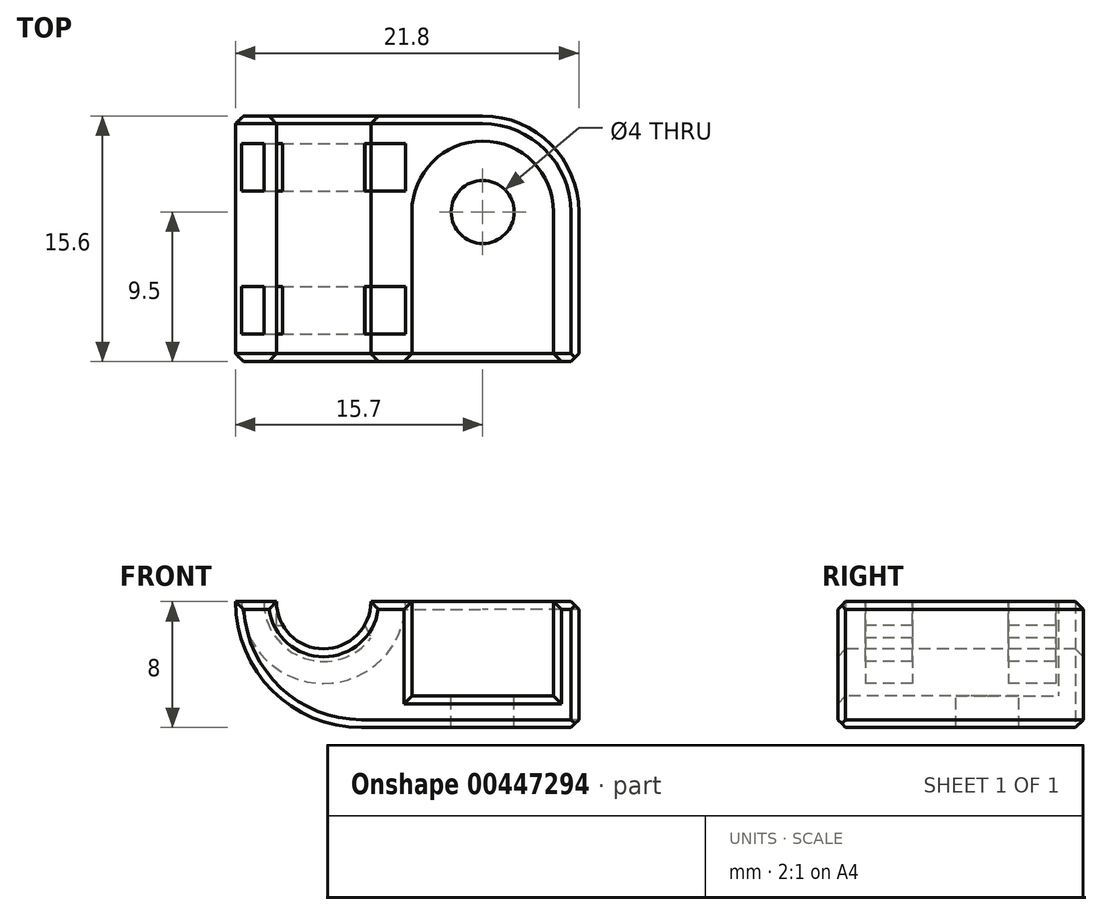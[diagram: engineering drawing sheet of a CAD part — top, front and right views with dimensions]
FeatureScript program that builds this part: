
annotation { "Feature Type Name" : "Feature", "Feature Type Description" : "" }
export const myFeature = defineFeature(function(context is Context, id is Id, definition is map)
    precondition{}
    {
        {
            var Q0;
            Q0=qCreatedBy(makeId("Top.planeOp"),FACE);
            var sketch = newSketch(context, id + "F0", { "sketchPlane" : qUnion([Q0])});
            skCircle(sketch, "E0", {"center": v(0, 0) * mm, "radius": 4.5 * mm});
            skLineSegment(sketch, "E1", {"start": v(-4.5, 0) * mm, "end": v(-4.5, -9.5) * mm});
            skLineSegment(sketch, "E2", {"start": v(-4.5, -9.5) * mm, "end": v(4.5, -9.5) * mm});
            skLineSegment(sketch, "E3", {"start": v(4.5, -9.5) * mm, "end": v(4.5, 0) * mm});
            skCircle(sketch, "E4", {"center": v(0, 0) * mm, "radius": 2 * mm});
            skSolve(sketch);
        }
        {
            var Q0;
            Q0=makeQuery(id+"F0.imprint","IMPRINT",FACE,{"disambiguationData":[TD([[makeQuery(id+"F0.imprint","IMPRINT",EDGE,{"derivedFrom":sQuery(id+"F0.wireOp",EDGE,"E4")}),-1.0]])]});
            var Q1;
            {var subQ0=sQuery(id+"F0.wireOp",EDGE,"E1");Q1=makeQuery(id+"F0.imprint","IMPRINT",FACE,{"disambiguationData":[TD([[makeQuery(id+"F0.imprint","IMPRINT",EDGE,{"derivedFrom":subQ0}),1.0]])]});}
            extrude(context, id + "F1", {"entities" : qUnion([Q0, Q1]), "depth" : 6 * mm});
        }
        {
            var Q0;
            Q0=qCreatedBy(makeId("Top.planeOp"),FACE);
            var sketch = newSketch(context, id + "F2", { "sketchPlane" : qUnion([Q0])});
            skLineSegment(sketch, "E5.bottom", {"start": v(6.1, -9.5) * mm, "end": v(-15.7, -9.5) * mm});
            skLineSegment(sketch, "E5.top", {"start": v(0, 6.1) * mm, "end": v(-15.7, 6.1) * mm});
            skLineSegment(sketch, "E5.left", {"start": v(6.1, -9.5) * mm, "end": v(6.1, 0) * mm});
            skLineSegment(sketch, "E5.right", {"start": v(-15.7, -9.5) * mm, "end": v(-15.7, 6.1) * mm});
            skPoint(sketch, "E6.visualSharp", {"position": v(6.1, 6.1) * mm});
            skArc(sketch, "E6.filletArc", {"start": v(6.1, 0) * mm, "mid": v(4.31, 4.31) * mm, "end": v(0, 6.1) * mm});
            skSolve(sketch);
        }
        {
            var Q0;
            Q0=makeQuery(id+"F2.imprint","IMPRINT",FACE,{"disambiguationData":[TD([[makeQuery(id+"F2.imprint","IMPRINT",EDGE,{"derivedFrom":sQuery(id+"F2.wireOp",EDGE,"E5.bottom")}),-1.0]])]});
            extrude(context, id + "F3", {"entities" : qUnion([Q0]), "depth" : 6 * mm, "hasSecondDirection" : true, "secondDirectionOppositeDirection" : true, "secondDirectionDepth" : 2 * mm});
        }
        {
            var Q0;
            Q0=makeQuery(id+"F3.opExtrude","SWEPT_FACE",FACE,{"disambiguationData":[OSD([sQuery(id+"F2.wireOp",EDGE,"E5.bottom")])]});
            var sketch = newSketch(context, id + "F4", { "sketchPlane" : qUnion([Q0])});
            skCircle(sketch, "E7", {"center": v(-10.1, 6) * mm, "radius": 3 * mm});
            skSolve(sketch);
        }
        {
            var Q0;
            {var subQ0=sQuery(id+"F4.wireOp",EDGE,"E7");var subQ1=makeQuery(id+"F3.opExtrude","CAP_EDGE",EDGE,{"disambiguationData":[OSD([sQuery(id+"F2.wireOp",EDGE,"E5.bottom")])],"isStart":false});var subQ2=makeQuery(id+"F4.imprint","INTERSECT",VERTEX,{"disambiguationData":[OD(0.0)],"derivedFrom":[subQ1,subQ0]});Q0=makeQuery(id+"F4.imprint","IMPRINT",FACE,{"disambiguationData":[TD([[makeQuery(id+"F4.imprint","IMPRINT",EDGE,{"disambiguationData":[TD([[subQ2,1.0]])],"derivedFrom":subQ0}),1.0]])]});}
            extrude(context, id + "F5", {"entities" : qUnion([Q0]), "operationType" : NewBodyOperationType.REMOVE, "oppositeDirection" : true, "depth" : 25 * mm});
        }
        {
            var Q0;
            {var subQ0=sQuery(id+"F2.wireOp",EDGE,"E5.bottom");var subQ1=sQuery(id+"F2.wireOp",EDGE,"E5.right");var subQ2=sQuery(id+"F2.wireOp",EDGE,"E5.top");Q0=makeQuery(id+"F5.boolean.opBoolean","SPLIT",FACE,{"disambiguationData":[TD([makeQuery(id+"F3.opExtrude","SWEPT_FACE",FACE,{"disambiguationData":[OSD([subQ1])]})])],"derivedFrom":makeQuery(id+"F3.opExtrude","CAP_FACE",FACE,{"disambiguationData":[OSD([subQ0,subQ2,sQuery(id+"F2.wireOp",EDGE,"E5.left"),subQ1,sQuery(id+"F2.wireOp",EDGE,"E6.filletArc")])],"isStart":false})});}
            var sketch = newSketch(context, id + "F6", { "sketchPlane" : qUnion([Q0])});
            skLineSegment(sketch, "E8", {"start": v(-10.1, 8.12) * mm, "end": v(-10.1, -13.09) * mm, "construction": true});
            skLineSegment(sketch, "E9.bottom", {"start": v(-15.3, -4.74) * mm, "end": v(-13.9, -4.74) * mm});
            skLineSegment(sketch, "E9.top", {"start": v(-15.3, -7.74) * mm, "end": v(-13.9, -7.74) * mm});
            skLineSegment(sketch, "E9.left", {"start": v(-15.3, -4.74) * mm, "end": v(-15.3, -7.74) * mm});
            skLineSegment(sketch, "E9.right", {"start": v(-13.9, -4.74) * mm, "end": v(-13.9, -7.74) * mm});
            skLineSegment(sketch, "E10.bottom", {"start": v(-15.3, 4.34) * mm, "end": v(-13.9, 4.34) * mm});
            skLineSegment(sketch, "E10.top", {"start": v(-15.3, 1.34) * mm, "end": v(-13.9, 1.34) * mm});
            skLineSegment(sketch, "E10.left", {"start": v(-15.3, 4.34) * mm, "end": v(-15.3, 1.34) * mm});
            skLineSegment(sketch, "E10.right", {"start": v(-13.9, 4.34) * mm, "end": v(-13.9, 1.34) * mm});
            skLineSegment(sketch, "E11", {"start": v(-15.7, -1.7) * mm, "end": v(-11.9, -1.7) * mm, "construction": true});
            skSolve(sketch);
        }
        {
            var Q0;
            Q0=makeQuery(id+"F6.imprint","IMPRINT",FACE,{"disambiguationData":[TD([[makeQuery(id+"F6.imprint","IMPRINT",EDGE,{"derivedFrom":sQuery(id+"F6.wireOp",EDGE,"E10.bottom")}),-1.0]])]});
            var Q1;
            Q1=makeQuery(id+"F6.imprint","IMPRINT",FACE,{"disambiguationData":[TD([[makeQuery(id+"F6.imprint","IMPRINT",EDGE,{"derivedFrom":sQuery(id+"F6.wireOp",EDGE,"E9.bottom")}),-1.0]])]});
            var Q2;
            Q2=sQuery(id+"F6.wireOp",EDGE,"E8");
            revolve(context, id + "F7", {"operationType" : NewBodyOperationType.REMOVE, "entities" : qUnion([Q0, Q1]), "axis" : qUnion([Q2]), "revolveType" : RevolveType.FULL, "oppositeDirection" : true});
        }
        {
            var Q0;
            Q0=makeQuery(id+"F1.opExtrude","SWEPT_BODY",BODY,{"disambiguationData":[OSD([sQuery(id+"F0.wireOp",EDGE,"E0"),sQuery(id+"F0.wireOp",EDGE,"E1"),sQuery(id+"F0.wireOp",EDGE,"E2"),sQuery(id+"F0.wireOp",EDGE,"E3"),sQuery(id+"F0.wireOp",EDGE,"E4")])]});
            var Q1;
            Q1=makeQuery(id+"F3.opExtrude","SWEPT_BODY",BODY,{"disambiguationData":[OSD([sQuery(id+"F2.wireOp",EDGE,"E5.bottom"),sQuery(id+"F2.wireOp",EDGE,"E5.top"),sQuery(id+"F2.wireOp",EDGE,"E5.left"),sQuery(id+"F2.wireOp",EDGE,"E5.right"),sQuery(id+"F2.wireOp",EDGE,"E6.filletArc")])]});
            booleanBodies(context, id + "F8", {"operationType" : BooleanOperationType.SUBTRACTION, "tools" : qUnion([Q0]), "targets" : qUnion([Q1])});
        }
        {
            var Q0;
            {var subQ0=sQuery(id+"F2.wireOp",EDGE,"E6.filletArc");var subQ1=sQuery(id+"F2.wireOp",EDGE,"E5.left");var subQ2=sQuery(id+"F2.wireOp",EDGE,"E5.top");var subQ3=sQuery(id+"F2.wireOp",EDGE,"E5.bottom");Q0=makeQuery(id+"F8.opBoolean","SPLIT",FACE,{"disambiguationData":[TD([makeQuery(id+"F1.opExtrude","SWEPT_FACE",FACE,{"disambiguationData":[OSD([sQuery(id+"F0.wireOp",EDGE,"E4")])]})])],"derivedFrom":makeQuery(id+"F5.boolean.opBoolean","SPLIT",FACE,{"disambiguationData":[TD([makeQuery(id+"F3.opExtrude","SWEPT_FACE",FACE,{"disambiguationData":[OSD([subQ1])]})])],"derivedFrom":makeQuery(id+"F3.opExtrude","CAP_FACE",FACE,{"disambiguationData":[OSD([subQ3,subQ2,subQ1,sQuery(id+"F2.wireOp",EDGE,"E5.right"),subQ0])],"isStart":false})})});}
            var Q1;
            {var subQ0=sQuery(id+"F2.wireOp",EDGE,"E6.filletArc");var subQ1=sQuery(id+"F2.wireOp",EDGE,"E5.left");var subQ2=sQuery(id+"F2.wireOp",EDGE,"E5.top");var subQ3=sQuery(id+"F2.wireOp",EDGE,"E5.bottom");Q1=makeQuery(id+"F8.opBoolean","SPLIT",FACE,{"disambiguationData":[TD([makeQuery(id+"F1.opExtrude","SWEPT_FACE",FACE,{"disambiguationData":[OSD([sQuery(id+"F0.wireOp",EDGE,"E4")])]})])],"derivedFrom":makeQuery(id+"F5.boolean.opBoolean","SPLIT",FACE,{"disambiguationData":[TD([makeQuery(id+"F3.opExtrude","SWEPT_FACE",FACE,{"disambiguationData":[OSD([subQ1])]})])],"derivedFrom":makeQuery(id+"F3.opExtrude","CAP_FACE",FACE,{"disambiguationData":[OSD([subQ3,subQ2,subQ1,sQuery(id+"F2.wireOp",EDGE,"E5.right"),subQ0])],"isStart":false})})});}
            extrude(context, id + "F9", {"entities" : qUnion([Q0, Q1]), "operationType" : NewBodyOperationType.REMOVE, "oppositeDirection" : true, "depth" : 25 * mm});
        }
        {
            var Q0;
            Q0=makeQuery(id+"F3.opExtrude","CAP_EDGE",EDGE,{"disambiguationData":[OSD([sQuery(id+"F2.wireOp",EDGE,"E5.right")])],"isStart":true});
            fillet(context, id + "F10", {"entities" : qUnion([Q0]), "radius" : 8 * mm, "tangentPropagation" : true, "allowEdgeOverflow" : false});
        }
        {
            var Q0;
            {var subQ0=sQuery(id+"F2.wireOp",EDGE,"E5.bottom");var subQ1=sQuery(id+"F2.wireOp",EDGE,"E5.right");var subQ2=sQuery(id+"F2.wireOp",EDGE,"E5.top");Q0=makeQuery(id+"F5.boolean.opBoolean","SPLIT",FACE,{"disambiguationData":[TD([makeQuery(id+"F3.opExtrude","SWEPT_FACE",FACE,{"disambiguationData":[OSD([subQ1])]})])],"derivedFrom":makeQuery(id+"F3.opExtrude","CAP_FACE",FACE,{"disambiguationData":[OSD([subQ0,subQ2,sQuery(id+"F2.wireOp",EDGE,"E5.left"),subQ1,sQuery(id+"F2.wireOp",EDGE,"E6.filletArc")])],"isStart":false})});}
            var sketch = newSketch(context, id + "F11", { "sketchPlane" : qUnion([Q0])});
            skPoint(sketch, "E12.oppositeSnap0", {"position": v(-14.6, 1.34) * mm});
            skLineSegment(sketch, "E12.bottom", {"start": v(-14.6, 4.34) * mm, "end": v(-5.6, 4.34) * mm});
            skLineSegment(sketch, "E12.top", {"start": v(-14.6, 1.34) * mm, "end": v(-5.6, 1.34) * mm});
            skLineSegment(sketch, "E12.left", {"start": v(-14.6, 4.34) * mm, "end": v(-14.6, 1.34) * mm});
            skLineSegment(sketch, "E12.right", {"start": v(-5.6, 4.34) * mm, "end": v(-5.6, 1.34) * mm});
            skPoint(sketch, "E13.oppositeSnap0", {"position": v(-14.6, -7.74) * mm});
            skLineSegment(sketch, "E13.bottom", {"start": v(-14.6, -4.74) * mm, "end": v(-5.57, -4.74) * mm});
            skLineSegment(sketch, "E13.top", {"start": v(-14.6, -7.74) * mm, "end": v(-5.57, -7.74) * mm});
            skLineSegment(sketch, "E13.left", {"start": v(-14.6, -4.74) * mm, "end": v(-14.6, -7.74) * mm});
            skLineSegment(sketch, "E13.right", {"start": v(-5.57, -4.74) * mm, "end": v(-5.57, -7.74) * mm});
            skSolve(sketch);
        }
        {
            var Q0;
            {var subQ0=sQuery(id+"F11.wireOp",EDGE,"E12.bottom");var subQ1=sQuery(id+"F2.wireOp",EDGE,"E5.bottom");var subQ4=sQuery(id+"F4.wireOp",EDGE,"E7");var subQ6=makeQuery(id+"F5.boolean.opBoolean","COPY",EDGE,{"derivedFrom":makeQuery(id+"F5.opExtrude","SWEPT_EDGE",EDGE,{"disambiguationData":[OSD([subQ1,subQ4]),TDD([makeQuery(id+"F4.imprint","INTERSECT",VERTEX,{"disambiguationData":[OD(1.0)],"derivedFrom":[makeQuery(id+"F3.opExtrude","CAP_EDGE",EDGE,{"disambiguationData":[OSD([subQ1])],"isStart":false}),subQ4]})])]})});var subQ7=makeQuery(id+"F11.imprint","INTERSECT",VERTEX,{"derivedFrom":[subQ6,subQ0]});Q0=makeQuery(id+"F11.imprint","IMPRINT",FACE,{"disambiguationData":[TD([[makeQuery(id+"F11.imprint","IMPRINT",EDGE,{"disambiguationData":[TD([[subQ7,-1.0]])],"derivedFrom":subQ6}),-1.0]])]});}
            var Q1;
            {var subQ0=sQuery(id+"F11.wireOp",EDGE,"E12.right");Q1=makeQuery(id+"F11.imprint","IMPRINT",FACE,{"disambiguationData":[TD([[makeQuery(id+"F11.imprint","IMPRINT",EDGE,{"derivedFrom":subQ0}),-1.0]])]});}
            var Q2;
            {var subQ0=sQuery(id+"F11.wireOp",EDGE,"E13.bottom");var subQ1=sQuery(id+"F2.wireOp",EDGE,"E5.bottom");var subQ4=sQuery(id+"F4.wireOp",EDGE,"E7");var subQ6=makeQuery(id+"F5.boolean.opBoolean","COPY",EDGE,{"derivedFrom":makeQuery(id+"F5.opExtrude","SWEPT_EDGE",EDGE,{"disambiguationData":[OSD([subQ1,subQ4]),TDD([makeQuery(id+"F4.imprint","INTERSECT",VERTEX,{"disambiguationData":[OD(1.0)],"derivedFrom":[makeQuery(id+"F3.opExtrude","CAP_EDGE",EDGE,{"disambiguationData":[OSD([subQ1])],"isStart":false}),subQ4]})])]})});var subQ7=makeQuery(id+"F11.imprint","INTERSECT",VERTEX,{"derivedFrom":[subQ6,subQ0]});Q2=makeQuery(id+"F11.imprint","IMPRINT",FACE,{"disambiguationData":[TD([[makeQuery(id+"F11.imprint","IMPRINT",EDGE,{"disambiguationData":[TD([[subQ7,-1.0]])],"derivedFrom":subQ6}),-1.0]])]});}
            var Q3;
            {var subQ0=sQuery(id+"F11.wireOp",EDGE,"E13.right");Q3=makeQuery(id+"F11.imprint","IMPRINT",FACE,{"disambiguationData":[TD([[makeQuery(id+"F11.imprint","IMPRINT",EDGE,{"derivedFrom":subQ0}),-1.0]])]});}
            extrude(context, id + "F12", {"entities" : qUnion([Q0, Q1, Q2, Q3]), "operationType" : NewBodyOperationType.REMOVE, "oppositeDirection" : true, "depth" : 1.5 * mm});
        }
        {
            var Q0;
            {var subQ0=sQuery(id+"F6.wireOp",EDGE,"E10.right");Q0=makeQuery(id+"F12.boolean.opBoolean","INTERSECT",EDGE,{"disambiguationData":[OD(1.0)],"derivedFrom":[makeQuery(id+"F7.boolean.opBoolean","COPY",FACE,{"derivedFrom":makeQuery(id+"F7.opRevolve","SWEPT_FACE",FACE,{"disambiguationData":[OSD([subQ0])]})}),makeQuery(id+"F12.opExtrude","CAP_FACE",FACE,{"disambiguationData":[OSD([sQuery(id+"F2.wireOp",EDGE,"E5.bottom"),sQuery(id+"F2.wireOp",EDGE,"E5.top"),sQuery(id+"F2.wireOp",EDGE,"E5.left"),sQuery(id+"F2.wireOp",EDGE,"E5.right"),sQuery(id+"F2.wireOp",EDGE,"E6.filletArc"),subQ0,sQuery(id+"F11.wireOp",EDGE,"E12.bottom"),sQuery(id+"F11.wireOp",EDGE,"E12.top"),sQuery(id+"F11.wireOp",EDGE,"E12.right")])],"isStart":false})]});}
            var Q1;
            {var subQ0=sQuery(id+"F6.wireOp",EDGE,"E10.right");Q1=makeQuery(id+"F12.boolean.opBoolean","INTERSECT",EDGE,{"disambiguationData":[OD(0.0)],"derivedFrom":[makeQuery(id+"F7.boolean.opBoolean","COPY",FACE,{"derivedFrom":makeQuery(id+"F7.opRevolve","SWEPT_FACE",FACE,{"disambiguationData":[OSD([subQ0])]})}),makeQuery(id+"F12.opExtrude","CAP_FACE",FACE,{"disambiguationData":[OSD([sQuery(id+"F2.wireOp",EDGE,"E5.bottom"),sQuery(id+"F2.wireOp",EDGE,"E5.top"),sQuery(id+"F2.wireOp",EDGE,"E5.left"),sQuery(id+"F2.wireOp",EDGE,"E5.right"),sQuery(id+"F2.wireOp",EDGE,"E6.filletArc"),subQ0,sQuery(id+"F11.wireOp",EDGE,"E12.bottom"),sQuery(id+"F11.wireOp",EDGE,"E12.top"),sQuery(id+"F11.wireOp",EDGE,"E12.right")])],"isStart":false})]});}
            var Q2;
            {var subQ0=sQuery(id+"F6.wireOp",EDGE,"E9.right");Q2=makeQuery(id+"F12.boolean.opBoolean","INTERSECT",EDGE,{"disambiguationData":[OD(1.0)],"derivedFrom":[makeQuery(id+"F7.boolean.opBoolean","COPY",FACE,{"derivedFrom":makeQuery(id+"F7.opRevolve","SWEPT_FACE",FACE,{"disambiguationData":[OSD([subQ0])]})}),makeQuery(id+"F12.opExtrude","CAP_FACE",FACE,{"disambiguationData":[OSD([sQuery(id+"F2.wireOp",EDGE,"E5.bottom"),sQuery(id+"F2.wireOp",EDGE,"E5.top"),sQuery(id+"F2.wireOp",EDGE,"E5.left"),sQuery(id+"F2.wireOp",EDGE,"E5.right"),sQuery(id+"F2.wireOp",EDGE,"E6.filletArc"),subQ0,sQuery(id+"F11.wireOp",EDGE,"E13.bottom"),sQuery(id+"F11.wireOp",EDGE,"E13.top"),sQuery(id+"F11.wireOp",EDGE,"E13.right")])],"isStart":false})]});}
            var Q3;
            {var subQ0=sQuery(id+"F6.wireOp",EDGE,"E9.right");Q3=makeQuery(id+"F12.boolean.opBoolean","INTERSECT",EDGE,{"disambiguationData":[OD(0.0)],"derivedFrom":[makeQuery(id+"F7.boolean.opBoolean","COPY",FACE,{"derivedFrom":makeQuery(id+"F7.opRevolve","SWEPT_FACE",FACE,{"disambiguationData":[OSD([subQ0])]})}),makeQuery(id+"F12.opExtrude","CAP_FACE",FACE,{"disambiguationData":[OSD([sQuery(id+"F2.wireOp",EDGE,"E5.bottom"),sQuery(id+"F2.wireOp",EDGE,"E5.top"),sQuery(id+"F2.wireOp",EDGE,"E5.left"),sQuery(id+"F2.wireOp",EDGE,"E5.right"),sQuery(id+"F2.wireOp",EDGE,"E6.filletArc"),subQ0,sQuery(id+"F11.wireOp",EDGE,"E13.bottom"),sQuery(id+"F11.wireOp",EDGE,"E13.top"),sQuery(id+"F11.wireOp",EDGE,"E13.right")])],"isStart":false})]});}
            chamfer(context, id + "F13", {"entities" : qUnion([Q0, Q1, Q2, Q3]), "width" : .5 * mm, "tangentPropagation" : true});
        }
        {
            var Q0;
            Q0=makeQuery(id+"F3.opExtrude","SWEPT_FACE",FACE,{"disambiguationData":[OSD([sQuery(id+"F2.wireOp",EDGE,"E5.bottom")])]});
            chamfer(context, id + "F14", {"entities" : qUnion([Q0]), "width" : .5 * mm, "tangentPropagation" : true});
        }
        {
            var Q0;
            Q0=makeQuery(id+"F3.opExtrude","SWEPT_FACE",FACE,{"disambiguationData":[OSD([sQuery(id+"F2.wireOp",EDGE,"E5.top")])]});
            chamfer(context, id + "F15", {"entities" : qUnion([Q0]), "width" : .5 * mm, "tangentPropagation" : true});
        }
    });
